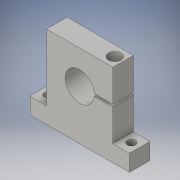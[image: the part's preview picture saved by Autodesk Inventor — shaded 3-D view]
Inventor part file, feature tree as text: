
AUTODESK INVENTOR PART (.ipt)
format: ipt  version: 2016 (Build 200138000, 138)  size: 144,896 bytes
history: native  units: in
note: dims shown in document units (in); Inventor stores cm internally (conversion verified against a paired STEP export)
features: sketch x4, extrude x2, hole x2
ambient origin geometry x8: Origin, YZ Plane, XZ Plane, XY Plane, X Axis, Y Axis, Z Axis, Center Point
bodies: Solid1 (feature_tree)
feature tree (8):
  extrude  "Extrusion1"  Depth=0.5in
  extrude  "Extrusion2"  Depth=2.0in
  hole  "Hole1"  [1 undecoded]
  hole  "Hole2"  [1 undecoded]
  sketch  "Sketch1"  dims[d0=0.5in d1=0.5in]
  sketch  "Sketch2"  dims[d2=3.0in d3=2.0in]
  sketch  "Sketch3"  dims[d4=0.5in d5=0.62in d6=0.0in]
  sketch  "Sketch4"  dims[d7=0.88in d8=1.0in d9=1.0in d10=0.06in d11=0.97in d12=0.62in d13=0.0in d14=0.31in d15=0.25in d16=0.25in d17=0.31in d18=0.25in d19=0.75in d20=0.375in d21=0.25in d22=0.5635in d23=1.0in d24=0.8108in d25=0.31in d26=0.25in d27=0.25in d28=0.75in d29=0.38in d30=0.31in d31=0.5635in d32=1.0in d33=0.8108in]
note: 2 required parameter values undecoded (feature->parameter linkage not recoverable at this tier; creation-order binding heuristic only, values carry confidence <= 0.55)
